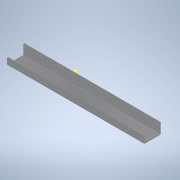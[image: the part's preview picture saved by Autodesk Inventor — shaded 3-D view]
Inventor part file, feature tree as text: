
AUTODESK INVENTOR PART (.ipt)
format: ipt  version: 2020 (Build 240168000, 168)  size: 507,904 bytes
history: native  units: in
note: dims shown in document units (in); Inventor stores cm internally (conversion verified against a paired STEP export)
features: extrude x1, fillet x1, sketch x1, other x1
ambient origin geometry x8: Origin, YZ Plane, XZ Plane, XY Plane, X Axis, Y Axis, Z Axis, Center Point
bodies: Solid1 (feature_tree)
feature tree (4):
  extrude  "Extrusion1"  Depth=0.375in
  fillet  "Fillet1"  Radius=0.375in
  sketch  "Sketch2"  dims[d1=0.375in d2=0.375in d3=0.375in d4=0.375in d5=0.375in d6=0.7874in d8=6.5625in d9=0.3937in d11=1.0in d13=0.375in d14=27.0in d15=13.5in d16=0.0in d17=0.0in d18=0.125in]
  other  "_AM14U3 End Sheet Rev1_-_LPattern4_"
